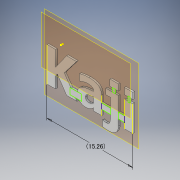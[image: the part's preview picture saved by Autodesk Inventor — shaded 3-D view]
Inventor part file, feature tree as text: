
AUTODESK INVENTOR PART (.ipt)
format: ipt  version: 2019.3 (Build 233278000, 278)  size: 217,600 bytes
history: native  units: in
note: dims shown in document units (in); Inventor stores cm internally (conversion verified against a paired STEP export)
features: extrude x3, other x2, sketch x2
ambient origin geometry x8: Origin, YZ Plane, XZ Plane, XY Plane, X Axis, Y Axis, Z Axis, Center Point
bodies: Body1 (feature_tree)
feature tree (7):
  other  "ソリッド1"
  sketch  "スケッチ1"
  extrude  "押し出し1"  Depth=0.0118in TaperAngle=0.0deg
  other  "作業平面1"
  sketch  "スケッチ4"
  extrude  "押し出し3"  Depth=0.0118in
  extrude  "押し出し4"  Depth=0.6008in
